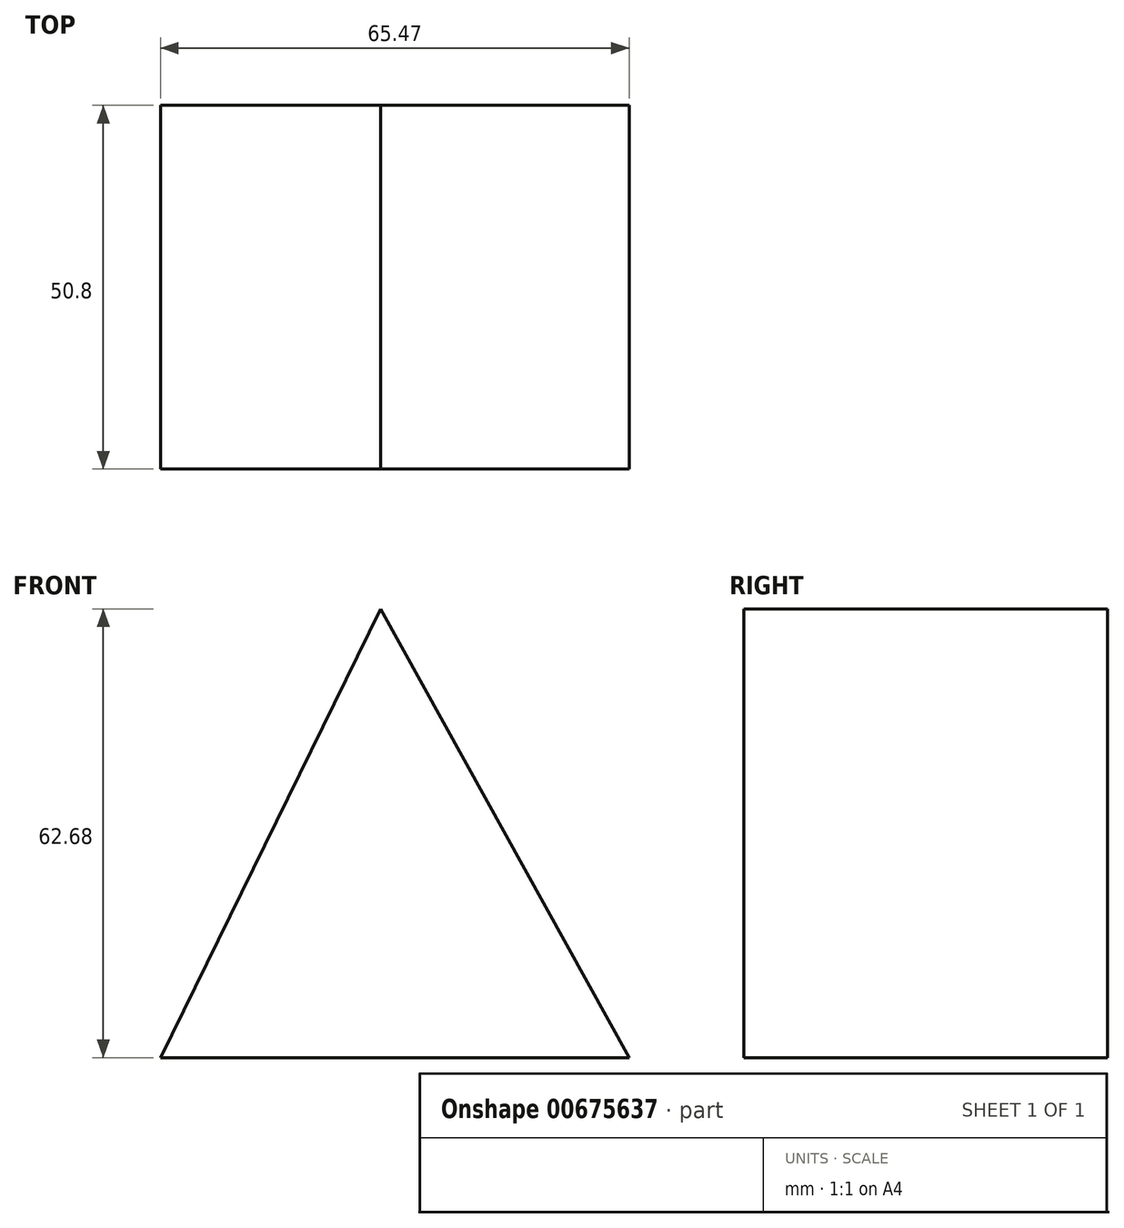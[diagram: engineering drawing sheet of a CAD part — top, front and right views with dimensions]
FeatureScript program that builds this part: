
annotation { "Feature Type Name" : "Feature", "Feature Type Description" : "" }
export const myFeature = defineFeature(function(context is Context, id is Id, definition is map)
    precondition{}
    {
        {
            var Q0;
            Q0=qCreatedBy(makeId("Front.planeOp"),FACE);
            var sketch = newSketch(context, id + "F0", { "sketchPlane" : qUnion([Q0])});
            skLineSegment(sketch, "E0", {"start": v(0, 0) * mm, "end": v(-34.69, 62.68) * mm});
            skLineSegment(sketch, "E1", {"start": v(-34.69, 62.68) * mm, "end": v(-65.47, 0) * mm});
            skLineSegment(sketch, "E2", {"start": v(-65.47, 0) * mm, "end": v(0, 0) * mm});
            skSolve(sketch);
        }
        {
            var Q0;
            Q0=makeQuery(id+"F0.imprint","IMPRINT",FACE,{"disambiguationData":[TD([[makeQuery(id+"F0.imprint","IMPRINT",EDGE,{"derivedFrom":sQuery(id+"F0.wireOp",EDGE,"E0")}),1.0]])]});
            extrude(context, id + "F1", {"entities" : qUnion([Q0]), "depth" : 50.8 * mm, "offsetDistance" : 25.4 * mm});
        }
    });
